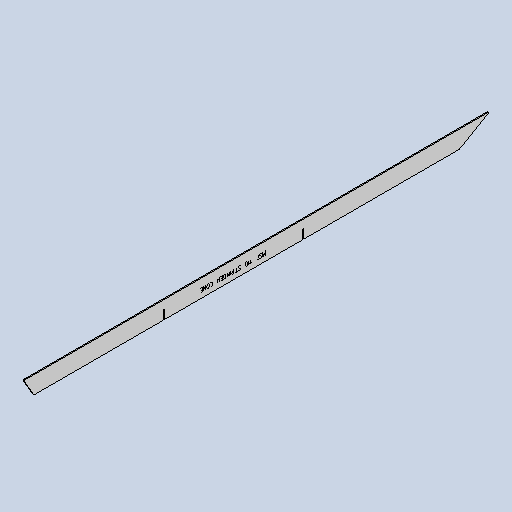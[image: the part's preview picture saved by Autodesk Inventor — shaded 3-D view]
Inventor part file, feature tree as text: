
AUTODESK INVENTOR PART (.ipt)
format: ipt  version: 2025 (Build 290162010, 162A)  size: 402,944 bytes
history: native  units: mm
features: other x5, sketch x3, sheet_metal_op x1, chamfer x1, extrude x1
ambient origin geometry x8: Origin, YZ Plane, XZ Plane, XY Plane, X Axis, Y Axis, Z Axis, Center Point
bodies: Body1 (feature_tree)
feature tree (11):
  sheet_metal_op  "Face1"
  other  "Corner Chamfer1"
  chamfer  "Corner Round1"
  extrude  "Extrusion1"  Depth=1330.0mm
  other  "Mark1"
  other  "A-Side Definition"
  sketch  "Sketch2"  dims[d3=380.0mm d6=380.0mm d7=380.0mm d28=1330.0mm]
  other  "Plate2"
  sketch  "Sketch3"  dims[d29=50.0mm]
  sketch  "Sketch4"  dims[d30=3.0mm d31=6.335545mm d32=10.47518mm d33=3.0mm d34=6.0mm d35=45.0deg d36=10.47518mm d37=6.0mm d38=219.04mm d39=26.0mm d40=3.0mm d41=399.0mm d42=798.0mm d43=3.0mm d44=26.0mm d45=0.0mm d46=0.0mm]
  other  "Definition1"
